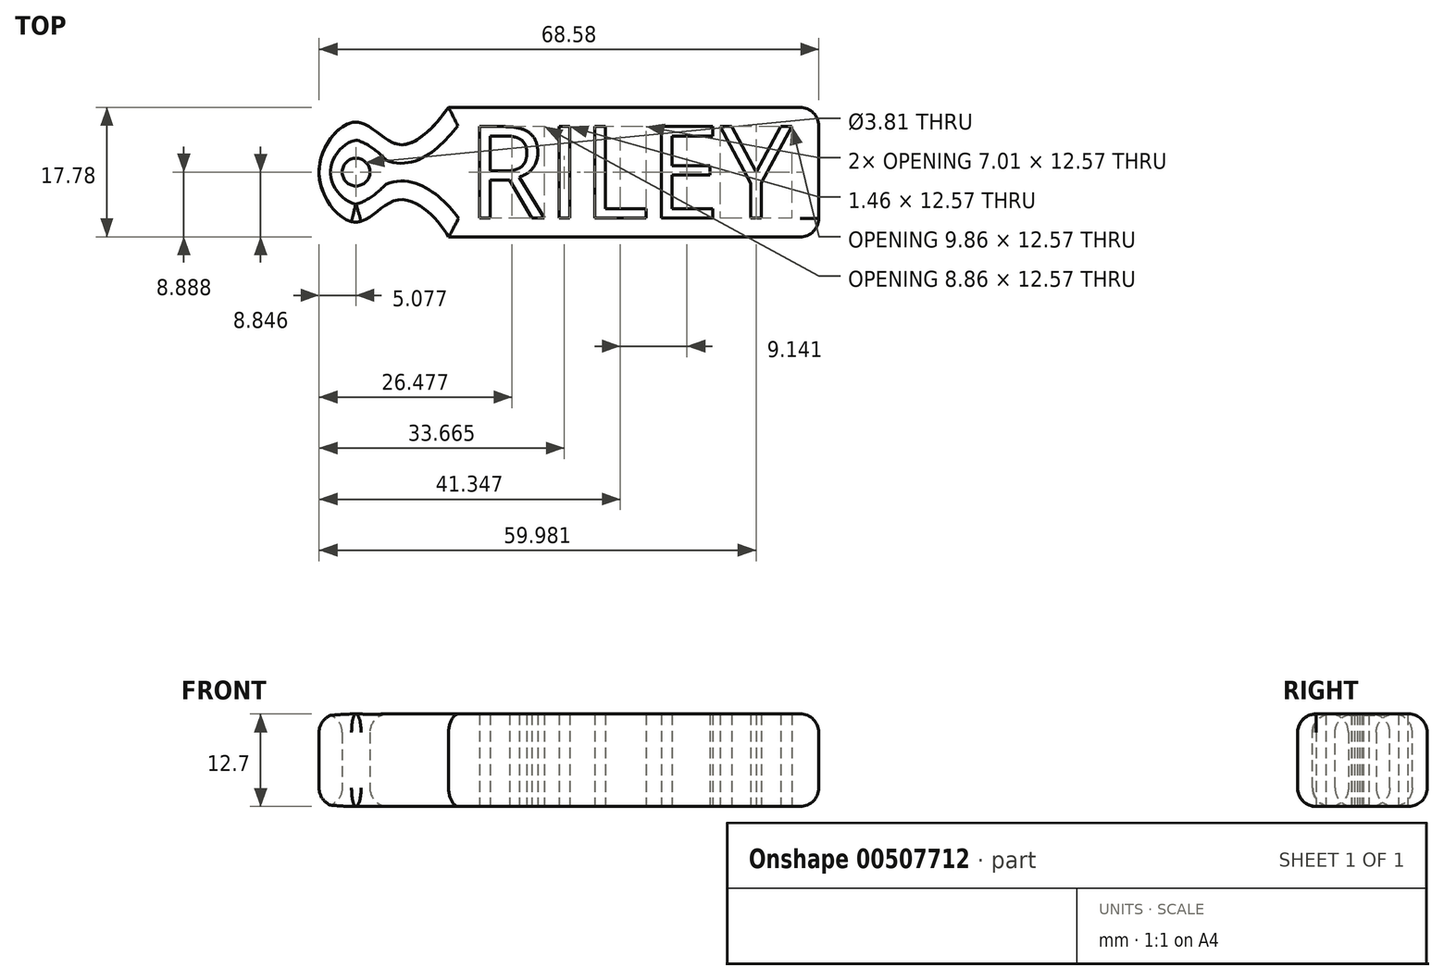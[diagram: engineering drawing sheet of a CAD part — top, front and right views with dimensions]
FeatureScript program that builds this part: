
annotation { "Feature Type Name" : "Feature", "Feature Type Description" : "" }
export const myFeature = defineFeature(function(context is Context, id is Id, definition is map)
    precondition{}
    {
        {
            var Q0;
            Q0=qCreatedBy(makeId("Top.planeOp"),FACE);
            var sketch = newSketch(context, id + "F0", { "sketchPlane" : qUnion([Q0])});
            skLineSegment(sketch, "E0.bottom", {"start": v(-5.18, 15.75) * mm, "end": v(43.08, 15.75) * mm});
            skLineSegment(sketch, "E0.top", {"start": v(-5.18, -2.03) * mm, "end": v(43.08, -2.03) * mm});
            skLineSegment(sketch, "E0.left", {"start": v(-5.18, 15.75) * mm, "end": v(-5.18, -2.03) * mm});
            skLineSegment(sketch, "E0.right", {"start": v(45.62, 13.2) * mm, "end": v(45.62, 0.5) * mm});
            skText(sketch, "E1", { "text": "RILEY", "fontName": "OpenSans-Regular.ttf"});
            skFitSpline(sketch, "E2", {"points": [v(-5.18, -2.03) * mm, v(-12.17, 3.05) * mm, v(-17.88, 0) * mm, v(-22.96, 6.86) * mm, v(-17.88, 13.72) * mm, v(-12.17, 10.67) * mm, v(-5.18, 15.75) * mm], "startDerivative": vector(-29.46, 49.57) * mm, "endDerivative": vector(36.7, 50.82) * mm});
            skCircle(sketch, "E3", {"center": v(-17.88, 6.86) * mm, "radius": 1.9 * mm});
            skPoint(sketch, "E4.visualSharp", {"position": v(45.62, 15.75) * mm});
            skArc(sketch, "E4.filletArc", {"start": v(45.62, 13.2) * mm, "mid": v(44.87, 15) * mm, "end": v(43.08, 15.75) * mm});
            skPoint(sketch, "E5.visualSharp", {"position": v(45.62, -2.03) * mm});
            skArc(sketch, "E5.filletArc", {"start": v(43.08, -2.03) * mm, "mid": v(44.87, -1.29) * mm, "end": v(45.62, 0.5) * mm});
            const initialGuessF0  = {"E1": [-0.00264, 0.00053, 1, 0, 0.01268]};
            skSetInitialGuess(sketch, initialGuessF0);
            skSolve(sketch);
        }
        {
            var Q0;
            Q0=makeQuery(id+"F0.imprint","IMPRINT",FACE,{"disambiguationData":[TD([[makeQuery(id+"F0.imprint","IMPRINT",EDGE,{"derivedFrom":sQuery(id+"F0.wireOp",EDGE,"E0.bottom")}),-1.0]])]});
            var Q1;
            Q1=makeQuery(id+"F0.imprint","IMPRINT",FACE,{"disambiguationData":[TD([[makeQuery(id+"F0.imprint","IMPRINT",EDGE,{"derivedFrom":sQuery(id+"F0.wireOp",EDGE,"E1.sketch_text.stroke-11")}),1.0]])]});
            extrude(context, id + "F1", {"entities" : qUnion([Q0, Q1]), "depth" : 12.7 * mm});
        }
        {
            var Q0;
            Q0=makeQuery(id+"F0.imprint","IMPRINT",FACE,{"disambiguationData":[TD([[makeQuery(id+"F0.imprint","IMPRINT",EDGE,{"derivedFrom":sQuery(id+"F0.wireOp",EDGE,"E0.left")}),-1.0]])]});
            extrude(context, id + "F2", {"entities" : qUnion([Q0]), "operationType" : NewBodyOperationType.ADD, "depth" : 12.7 * mm});
        }
        {
            var Q0;
            Q0=makeQuery(id+"F2.opExtrude","CAP_EDGE",EDGE,{"disambiguationData":[OSD([sQuery(id+"F0.wireOp",EDGE,"E3")])],"isStart":true});
            var Q1;
            Q1=makeQuery(id+"F2.opExtrude","CAP_EDGE",EDGE,{"disambiguationData":[OSD([sQuery(id+"F0.wireOp",EDGE,"E3")])],"isStart":false});
            var Q2;
            Q2=makeQuery(id+"F2.opExtrude","CAP_EDGE",EDGE,{"disambiguationData":[OSD([sQuery(id+"F0.wireOp",EDGE,"E2")])],"isStart":false});
            var Q3;
            Q3=makeQuery(id+"F2.opExtrude","CAP_EDGE",EDGE,{"disambiguationData":[OSD([sQuery(id+"F0.wireOp",EDGE,"E2")])],"isStart":true});
            var Q4;
            Q4=makeQuery(id+"F1.opExtrude","CAP_EDGE",EDGE,{"disambiguationData":[OSD([sQuery(id+"F0.wireOp",EDGE,"E0.bottom")])],"isStart":true});
            var Q5;
            Q5=makeQuery(id+"F1.opExtrude","CAP_EDGE",EDGE,{"disambiguationData":[OSD([sQuery(id+"F0.wireOp",EDGE,"E0.bottom")])],"isStart":false});
            fillet(context, id + "F3", {"entities" : qUnion([Q0, Q1, Q2, Q3, Q4, Q5]), "radius" : 2.54 * mm, "tangentPropagation" : true, "allowEdgeOverflow" : false});
        }
    });
